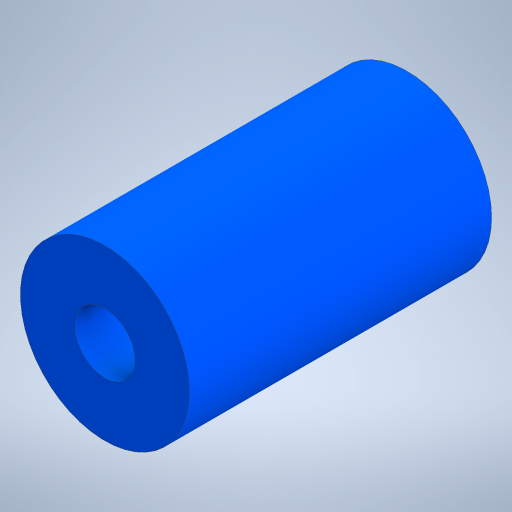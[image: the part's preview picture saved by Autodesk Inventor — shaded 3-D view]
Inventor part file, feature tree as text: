
AUTODESK INVENTOR PART (.ipt)
format: ipt  version: 2024 (Build 280153000, 153)  size: 217,088 bytes
history: native  units: in
note: dims shown in document units (in); Inventor stores cm internally (conversion verified against a paired STEP export)
features: extrude x3, sketch x3
ambient origin geometry x8: Origin, YZ Plane, XZ Plane, XY Plane, X Axis, Y Axis, Z Axis, Center Point
bodies: Solid1 (feature_tree)
feature tree (6):
  extrude  "Extrusion1"  Depth=0.9843in TaperAngle=0.0deg
  extrude  "Extrusion2"  Depth=0.9843in TaperAngle=0.0deg
  extrude  "Extrusion3"  Depth=0.4921in TaperAngle=0.0deg
  sketch  "Sketch1"  dims[d0=0.5512in d1=0.9843in d2=0.0in]
  sketch  "Sketch2"  dims[d3=0.1969in d4=0.9843in d5=0.0in]
  sketch  "Sketch3"  dims[d6=0.315in d7=0.4921in d8=0.0in]
